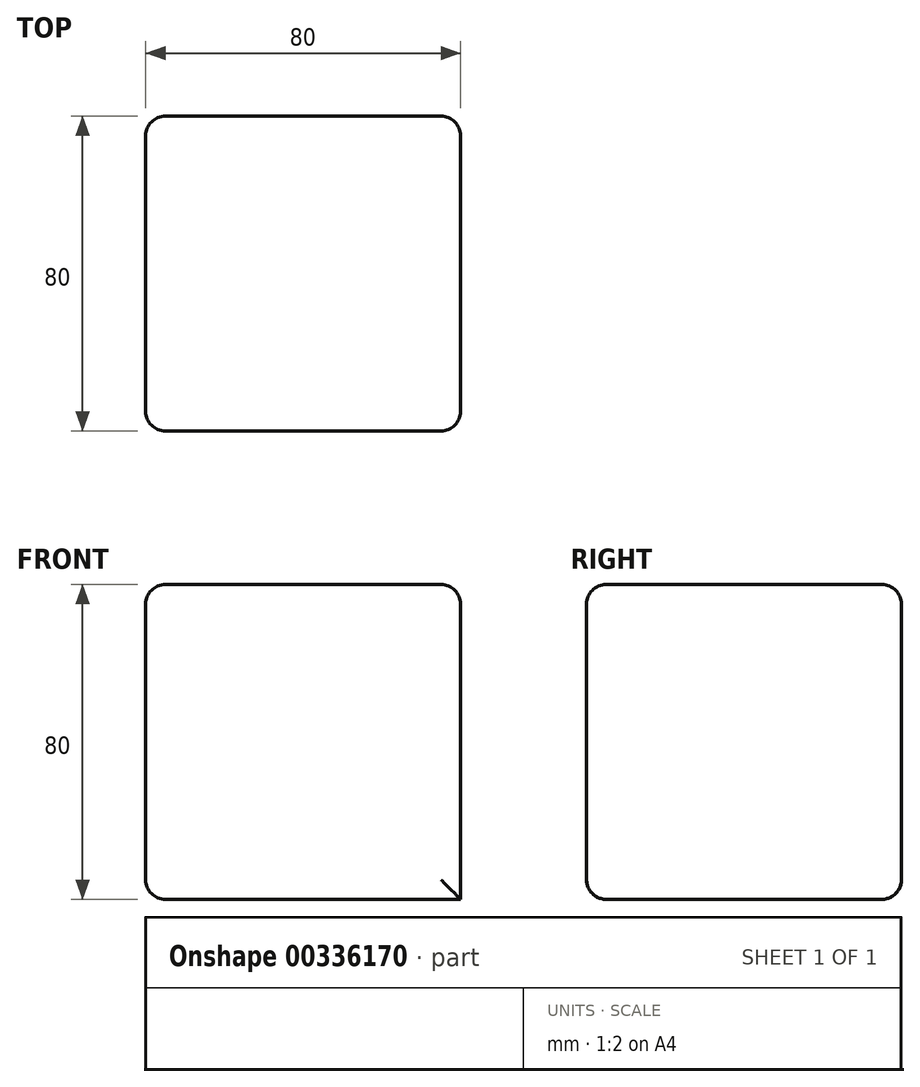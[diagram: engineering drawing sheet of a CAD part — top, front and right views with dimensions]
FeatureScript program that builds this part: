
annotation { "Feature Type Name" : "Feature", "Feature Type Description" : "" }
export const myFeature = defineFeature(function(context is Context, id is Id, definition is map)
    precondition{}
    {
        {
            var Q0;
            Q0=qCreatedBy(makeId("Top.planeOp"),FACE);
            var sketch = newSketch(context, id + "F0", { "sketchPlane" : qUnion([Q0])});
            skLineSegment(sketch, "E0.bottom", {"start": v(-40, 40) * mm, "end": v(40, 40) * mm});
            skLineSegment(sketch, "E0.top", {"start": v(-40, -40) * mm, "end": v(40, -40) * mm});
            skLineSegment(sketch, "E0.left", {"start": v(-40, 40) * mm, "end": v(-40, -40) * mm});
            skLineSegment(sketch, "E0.right", {"start": v(40, 40) * mm, "end": v(40, -40) * mm});
            skPoint(sketch, "E0.middle", {"position": v(0, 0) * mm});
            skSolve(sketch);
        }
        {
            var Q0;
            Q0=makeQuery(id+"F0.imprint","IMPRINT",FACE,{"disambiguationData":[TD([[makeQuery(id+"F0.imprint","IMPRINT",EDGE,{"derivedFrom":sQuery(id+"F0.wireOp",EDGE,"E0.bottom")}),-1.0]])]});
            extrude(context, id + "F1", {"entities" : qUnion([Q0]), "endBound" : BoundingType.SYMMETRIC, "depth" : 80 * mm});
        }
        {
            var Q0;
            Q0=makeQuery(id+"F1.opExtrude","CAP_FACE",FACE,{"disambiguationData":[OSD([sQuery(id+"F0.wireOp",EDGE,"E0.bottom"),sQuery(id+"F0.wireOp",EDGE,"E0.top"),sQuery(id+"F0.wireOp",EDGE,"E0.left"),sQuery(id+"F0.wireOp",EDGE,"E0.right")])],"isStart":false});
            var Q1;
            Q1=makeQuery(id+"F1.opExtrude","SWEPT_FACE",FACE,{"disambiguationData":[OSD([sQuery(id+"F0.wireOp",EDGE,"E0.top")])]});
            var Q2;
            Q2=makeQuery(id+"F1.opExtrude","SWEPT_FACE",FACE,{"disambiguationData":[OSD([sQuery(id+"F0.wireOp",EDGE,"E0.bottom")])]});
            var Q3;
            Q3=makeQuery(id+"F1.opExtrude","SWEPT_FACE",FACE,{"disambiguationData":[OSD([sQuery(id+"F0.wireOp",EDGE,"E0.left")])]});
            fillet(context, id + "F2", {"entities" : qUnion([Q0, Q1, Q2, Q3]), "radius" : 5 * mm, "tangentPropagation" : true, "allowEdgeOverflow" : false});
        }
    });
